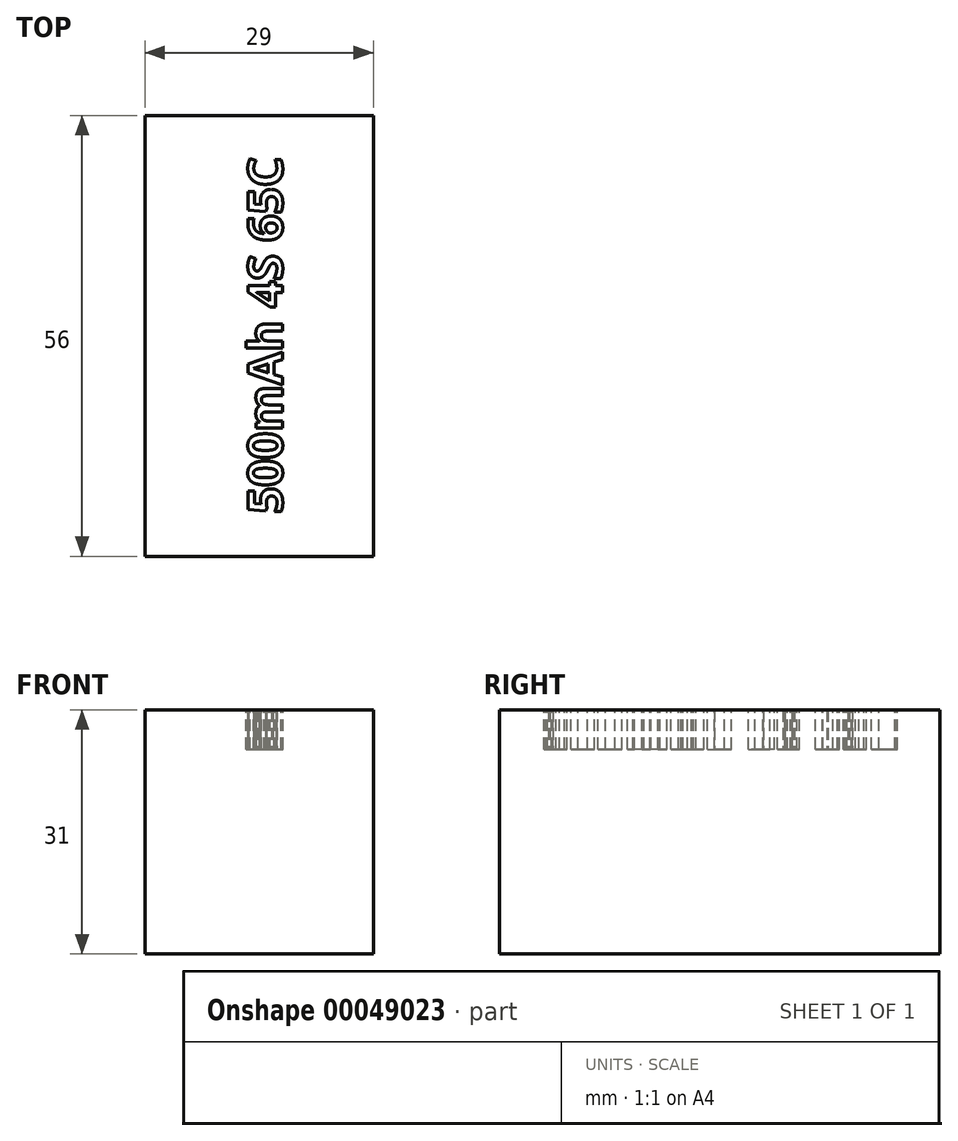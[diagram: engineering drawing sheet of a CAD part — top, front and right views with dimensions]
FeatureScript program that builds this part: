
annotation { "Feature Type Name" : "Feature", "Feature Type Description" : "" }
export const myFeature = defineFeature(function(context is Context, id is Id, definition is map)
    precondition{}
    {
        {
            var Q0;
            Q0=qCreatedBy(makeId("Top.planeOp"),FACE);
            var sketch = newSketch(context, id + "F0", { "sketchPlane" : qUnion([Q0])});
            skLineSegment(sketch, "E0.bottom", {"start": v(14.5, 28) * mm, "end": v(-14.5, 28) * mm});
            skLineSegment(sketch, "E0.top", {"start": v(14.5, -28) * mm, "end": v(-14.5, -28) * mm});
            skLineSegment(sketch, "E0.left", {"start": v(14.5, 28) * mm, "end": v(14.5, -28) * mm});
            skLineSegment(sketch, "E0.right", {"start": v(-14.5, 28) * mm, "end": v(-14.5, -28) * mm});
            skPoint(sketch, "E0.middle", {"position": v(0, 0) * mm});
            skSolve(sketch);
        }
        {
            var Q0;
            Q0 = qSketchRegion(id + "F0", true);
            extrude(context, id + "F1", {"entities" : qUnion([Q0]), "depth" : 31 * mm});
        }
        {
            var Q0;
            Q0=makeQuery(id+"F1.opExtrude","CAP_FACE",FACE,{"disambiguationData":[OSD([sQuery(id+"F0.wireOp",EDGE,"E0.bottom"),sQuery(id+"F0.wireOp",EDGE,"E0.top"),sQuery(id+"F0.wireOp",EDGE,"E0.left"),sQuery(id+"F0.wireOp",EDGE,"E0.right")])],"isStart":false});
            var sketch = newSketch(context, id + "F2", { "sketchPlane" : qUnion([Q0])});
            skText(sketch, "E1", { "text": "500mAh 4S 65C", "fontName": "OpenSans-Bold.ttf"});
            const initialGuessF2  = {"E1": [0.00295, -0.02261, 0, 1, 0.00438]};
            skSetInitialGuess(sketch, initialGuessF2);
            skSolve(sketch);
        }
        {
            var Q0;
            Q0 = qSketchRegion(id + "F2", true);
            extrude(context, id + "F3", {"entities" : qUnion([Q0]), "operationType" : NewBodyOperationType.REMOVE, "oppositeDirection" : true, "depth" : 5 * mm});
        }
    });
